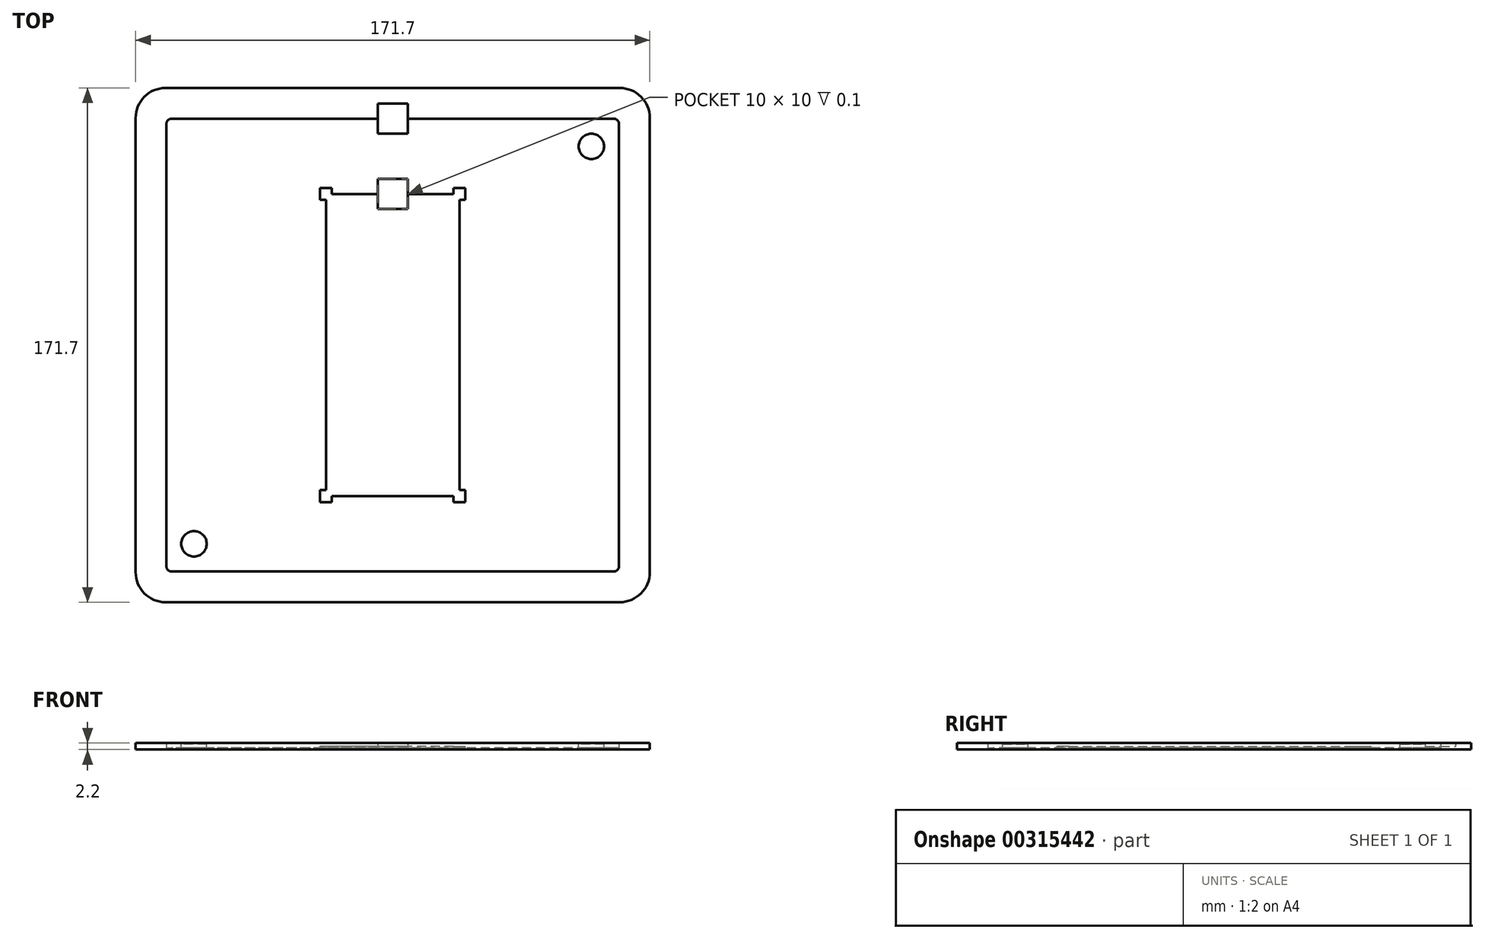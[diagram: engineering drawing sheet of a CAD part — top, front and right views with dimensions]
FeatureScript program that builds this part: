
annotation { "Feature Type Name" : "Feature", "Feature Type Description" : "" }
export const myFeature = defineFeature(function(context is Context, id is Id, definition is map)
    precondition{}
    {
        {
            var Q0;
            Q0=qCreatedBy(makeId("Top.planeOp"),FACE);
            var sketch = newSketch(context, id + "F0", { "sketchPlane" : qUnion([Q0])});
            skLineSegment(sketch, "E0.bottom", {"start": v(-75.85, 85.85) * mm, "end": v(75.85, 85.85) * mm});
            skLineSegment(sketch, "E0.top", {"start": v(-75.85, -85.85) * mm, "end": v(75.85, -85.85) * mm});
            skLineSegment(sketch, "E0.left", {"start": v(-85.85, 75.85) * mm, "end": v(-85.85, -75.85) * mm});
            skLineSegment(sketch, "E0.right", {"start": v(85.85, 75.85) * mm, "end": v(85.85, -75.85) * mm});
            skPoint(sketch, "E0.middle", {"position": v(0, 0) * mm});
            skLineSegment(sketch, "E1.bottom", {"start": v(-20.3, 50.45) * mm, "end": v(20.3, 50.45) * mm});
            skLineSegment(sketch, "E1.top", {"start": v(-20.3, -50.45) * mm, "end": v(20.3, -50.45) * mm});
            skLineSegment(sketch, "E1.left", {"start": v(-22.3, 48.45) * mm, "end": v(-22.3, -48.45) * mm});
            skLineSegment(sketch, "E1.right", {"start": v(22.3, 48.45) * mm, "end": v(22.3, -48.45) * mm});
            skPoint(sketch, "E2", {"position": v(0, 50.45) * mm});
            skPoint(sketch, "E3", {"position": v(-22.3, 0) * mm});
            skLineSegment(sketch, "E4.bottom", {"start": v(73.8, 75.6) * mm, "end": v(-73.8, 75.6) * mm});
            skLineSegment(sketch, "E4.top", {"start": v(73.8, -75.6) * mm, "end": v(-73.8, -75.6) * mm});
            skLineSegment(sketch, "E4.left", {"start": v(75.6, 73.8) * mm, "end": v(75.6, -73.8) * mm});
            skLineSegment(sketch, "E4.right", {"start": v(-75.6, 73.8) * mm, "end": v(-75.6, -73.8) * mm});
            skPoint(sketch, "E5.visualSharp", {"position": v(-85.85, 85.85) * mm});
            skArc(sketch, "E5.filletArc", {"start": v(-75.85, 85.85) * mm, "mid": v(-82.92, 82.92) * mm, "end": v(-85.85, 75.85) * mm});
            skPoint(sketch, "E6.visualSharp", {"position": v(-85.85, -85.85) * mm});
            skArc(sketch, "E6.filletArc", {"start": v(-85.85, -75.85) * mm, "mid": v(-82.92, -82.92) * mm, "end": v(-75.85, -85.85) * mm});
            skPoint(sketch, "E7.visualSharp", {"position": v(85.85, -85.85) * mm});
            skArc(sketch, "E7.filletArc", {"start": v(75.85, -85.85) * mm, "mid": v(82.92, -82.92) * mm, "end": v(85.85, -75.85) * mm});
            skPoint(sketch, "E8.visualSharp", {"position": v(85.85, 85.85) * mm});
            skArc(sketch, "E8.filletArc", {"start": v(85.85, 75.85) * mm, "mid": v(82.92, 82.92) * mm, "end": v(75.85, 85.85) * mm});
            skPoint(sketch, "E9.visualSharp", {"position": v(-75.6, 75.6) * mm});
            skArc(sketch, "E9.filletArc", {"start": v(-73.8, 75.6) * mm, "mid": v(-75.07, 75.07) * mm, "end": v(-75.6, 73.8) * mm});
            skPoint(sketch, "E10.visualSharp", {"position": v(75.6, 75.6) * mm});
            skArc(sketch, "E10.filletArc", {"start": v(75.6, 73.8) * mm, "mid": v(75.07, 75.07) * mm, "end": v(73.8, 75.6) * mm});
            skPoint(sketch, "E11.visualSharp", {"position": v(75.6, -75.6) * mm});
            skArc(sketch, "E11.filletArc", {"start": v(73.8, -75.6) * mm, "mid": v(75.07, -75.07) * mm, "end": v(75.6, -73.8) * mm});
            skPoint(sketch, "E12.visualSharp", {"position": v(-75.6, -75.6) * mm});
            skArc(sketch, "E12.filletArc", {"start": v(-75.6, -73.8) * mm, "mid": v(-75.07, -75.07) * mm, "end": v(-73.8, -75.6) * mm});
            skLineSegment(sketch, "E13.bottom", {"start": v(5, 70.6) * mm, "end": v(-5, 70.6) * mm});
            skLineSegment(sketch, "E13.top", {"start": v(5, 80.6) * mm, "end": v(-5, 80.6) * mm});
            skLineSegment(sketch, "E13.left", {"start": v(5, 70.6) * mm, "end": v(5, 80.6) * mm});
            skLineSegment(sketch, "E13.right", {"start": v(-5, 70.6) * mm, "end": v(-5, 80.6) * mm});
            skPoint(sketch, "E13.middle", {"position": v(0, 75.6) * mm});
            skLineSegment(sketch, "E14.bottom", {"start": v(-5, 55.45) * mm, "end": v(5, 55.45) * mm});
            skLineSegment(sketch, "E14.top", {"start": v(-5, 45.45) * mm, "end": v(5, 45.45) * mm});
            skLineSegment(sketch, "E14.left", {"start": v(-5, 55.45) * mm, "end": v(-5, 45.45) * mm});
            skLineSegment(sketch, "E14.right", {"start": v(5, 55.45) * mm, "end": v(5, 45.45) * mm});
            skLineSegment(sketch, "E15.bottom", {"start": v(24.3, 52.45) * mm, "end": v(20.3, 52.45) * mm});
            skLineSegment(sketch, "E15.top", {"start": v(24.3, 48.45) * mm, "end": v(22.3, 48.45) * mm});
            skLineSegment(sketch, "E15.left", {"start": v(24.3, 52.45) * mm, "end": v(24.3, 48.45) * mm});
            skLineSegment(sketch, "E15.right", {"start": v(20.3, 52.45) * mm, "end": v(20.3, 50.45) * mm});
            skPoint(sketch, "E15.middle", {"position": v(22.3, 50.45) * mm});
            skLineSegment(sketch, "E16", {"start": v(0, 50.45) * mm, "end": v(0, 38.86) * mm, "construction": true});
            skPoint(sketch, "E16.endSnap0", {"position": v(0, 45.45) * mm});
            skLineSegment(sketch, "E17", {"start": v(0, 0) * mm, "end": v(8.34, 0) * mm, "construction": true});
            skLineSegment(sketch, "E18.MirrorCS", {"start": v(-24.3, 52.45) * mm, "end": v(-24.3, 48.45) * mm});
            skLineSegment(sketch, "E19.MirrorCS", {"start": v(-24.3, 48.45) * mm, "end": v(-22.3, 48.45) * mm});
            skLineSegment(sketch, "E20.MirrorCS", {"start": v(-24.3, 52.45) * mm, "end": v(-20.3, 52.45) * mm});
            skLineSegment(sketch, "E21.MirrorCS", {"start": v(-20.3, 52.45) * mm, "end": v(-20.3, 50.45) * mm});
            skLineSegment(sketch, "E22.MirrorCS", {"start": v(24.3, -52.45) * mm, "end": v(24.3, -48.45) * mm});
            skLineSegment(sketch, "E23.MirrorCS", {"start": v(24.3, -48.45) * mm, "end": v(22.3, -48.45) * mm});
            skLineSegment(sketch, "E24.MirrorCS", {"start": v(20.3, -52.45) * mm, "end": v(20.3, -50.45) * mm});
            skLineSegment(sketch, "E25.MirrorCS", {"start": v(24.3, -52.45) * mm, "end": v(20.3, -52.45) * mm});
            skLineSegment(sketch, "E26.MirrorCS", {"start": v(-20.3, -52.45) * mm, "end": v(-20.3, -50.45) * mm});
            skLineSegment(sketch, "E27.MirrorCS", {"start": v(-24.3, -48.45) * mm, "end": v(-22.3, -48.45) * mm});
            skLineSegment(sketch, "E28.MirrorCS", {"start": v(-24.3, -52.45) * mm, "end": v(-20.3, -52.45) * mm});
            skLineSegment(sketch, "E29.MirrorCS", {"start": v(-24.3, -52.45) * mm, "end": v(-24.3, -48.45) * mm});
            skPoint(sketch, "E30.orphan", {"position": v(-22.3, 50.45) * mm});
            skPoint(sketch, "E31.orphan", {"position": v(-20.3, 48.45) * mm});
            skPoint(sketch, "E32.orphan", {"position": v(20.3, 48.45) * mm});
            skPoint(sketch, "E33.orphan", {"position": v(20.3, -48.45) * mm});
            skPoint(sketch, "E34.orphan", {"position": v(-22.3, -50.45) * mm});
            skPoint(sketch, "E35.orphan", {"position": v(-20.3, -48.45) * mm});
            skSolve(sketch);
        }
        {
            var Q0;
            Q0=makeQuery(id+"F0.imprint","IMPRINT",FACE,{"disambiguationData":[TD([[makeQuery(id+"F0.imprint","IMPRINT",EDGE,{"derivedFrom":sQuery(id+"F0.wireOp",EDGE,"E0.bottom")}),-1.0]])]});
            var Q1;
            Q1=makeQuery(id+"F0.imprint","IMPRINT",FACE,{"disambiguationData":[TD([[makeQuery(id+"F0.imprint","IMPRINT",EDGE,{"derivedFrom":sQuery(id+"F0.wireOp",EDGE,"E1.bottom")}),1.0]])]});
            var Q2;
            Q2=makeQuery(id+"F0.imprint","IMPRINT",FACE,{"disambiguationData":[TD([[makeQuery(id+"F0.imprint","IMPRINT",EDGE,{"derivedFrom":sQuery(id+"F0.wireOp",EDGE,"E1.bottom")}),-1.0]])]});
            var Q3;
            {var subQ5=sQuery(id+"F0.wireOp",EDGE,"E13.top");Q3=makeQuery(id+"F0.imprint","IMPRINT",FACE,{"disambiguationData":[TD([[makeQuery(id+"F0.imprint","IMPRINT",EDGE,{"derivedFrom":subQ5}),1.0]])]});}
            var Q4;
            {var subQ5=sQuery(id+"F0.wireOp",EDGE,"E14.bottom");Q4=makeQuery(id+"F0.imprint","IMPRINT",FACE,{"disambiguationData":[TD([[makeQuery(id+"F0.imprint","IMPRINT",EDGE,{"derivedFrom":subQ5}),-1.0]])]});}
            var Q5;
            {var subQ5=sQuery(id+"F0.wireOp",EDGE,"E13.bottom");Q5=makeQuery(id+"F0.imprint","IMPRINT",FACE,{"disambiguationData":[TD([[makeQuery(id+"F0.imprint","IMPRINT",EDGE,{"derivedFrom":subQ5}),-1.0]])]});}
            var Q6;
            {var subQ5=sQuery(id+"F0.wireOp",EDGE,"E14.top");Q6=makeQuery(id+"F0.imprint","IMPRINT",FACE,{"disambiguationData":[TD([[makeQuery(id+"F0.imprint","IMPRINT",EDGE,{"derivedFrom":subQ5}),1.0]])]});}
            extrude(context, id + "F1", {"entities" : qUnion([Q0, Q1, Q2, Q3, Q4, Q5, Q6]), "depth" : 1 * mm});
        }
        {
            var Q0;
            Q0=makeQuery(id+"F0.imprint","IMPRINT",FACE,{"disambiguationData":[TD([[makeQuery(id+"F0.imprint","IMPRINT",EDGE,{"derivedFrom":sQuery(id+"F0.wireOp",EDGE,"E0.bottom")}),-1.0]])]});
            var Q1;
            {var subQ5=sQuery(id+"F0.wireOp",EDGE,"E13.top");Q1=makeQuery(id+"F0.imprint","IMPRINT",FACE,{"disambiguationData":[TD([[makeQuery(id+"F0.imprint","IMPRINT",EDGE,{"derivedFrom":subQ5}),1.0]])]});}
            extrude(context, id + "F2", {"entities" : qUnion([Q0, Q1]), "operationType" : NewBodyOperationType.ADD, "depth" : (1 + 0.8 + 0.4) * mm});
        }
        {
            var Q0;
            Q0=makeQuery(id+"F0.imprint","IMPRINT",FACE,{"disambiguationData":[TD([[makeQuery(id+"F0.imprint","IMPRINT",EDGE,{"derivedFrom":sQuery(id+"F0.wireOp",EDGE,"E1.bottom")}),1.0]])]});
            var Q1;
            {var subQ5=sQuery(id+"F0.wireOp",EDGE,"E13.bottom");Q1=makeQuery(id+"F0.imprint","IMPRINT",FACE,{"disambiguationData":[TD([[makeQuery(id+"F0.imprint","IMPRINT",EDGE,{"derivedFrom":subQ5}),-1.0]])]});}
            var Q2;
            {var subQ5=sQuery(id+"F0.wireOp",EDGE,"E14.bottom");Q2=makeQuery(id+"F0.imprint","IMPRINT",FACE,{"disambiguationData":[TD([[makeQuery(id+"F0.imprint","IMPRINT",EDGE,{"derivedFrom":subQ5}),-1.0]])]});}
            extrude(context, id + "F3", {"entities" : qUnion([Q0, Q1, Q2]), "operationType" : NewBodyOperationType.ADD, "depth" : (1 + 0.8) * mm});
        }
        {
            var Q0;
            {var subQ5=sQuery(id+"F0.wireOp",EDGE,"E13.top");Q0=makeQuery(id+"F0.imprint","IMPRINT",FACE,{"disambiguationData":[TD([[makeQuery(id+"F0.imprint","IMPRINT",EDGE,{"derivedFrom":subQ5}),1.0]])]});}
            var Q1;
            {var subQ5=sQuery(id+"F0.wireOp",EDGE,"E13.bottom");Q1=makeQuery(id+"F0.imprint","IMPRINT",FACE,{"disambiguationData":[TD([[makeQuery(id+"F0.imprint","IMPRINT",EDGE,{"derivedFrom":subQ5}),-1.0]])]});}
            var Q2;
            Q2=makeQuery(id+"F2.opExtrude","CAP_FACE",FACE,{"disambiguationData":[OSD([sQuery(id+"F0.wireOp",EDGE,"E0.bottom"),sQuery(id+"F0.wireOp",EDGE,"E0.top"),sQuery(id+"F0.wireOp",EDGE,"E0.left"),sQuery(id+"F0.wireOp",EDGE,"E0.right"),sQuery(id+"F0.wireOp",EDGE,"E4.bottom"),sQuery(id+"F0.wireOp",EDGE,"E4.top"),sQuery(id+"F0.wireOp",EDGE,"E4.left"),sQuery(id+"F0.wireOp",EDGE,"E4.right"),sQuery(id+"F0.wireOp",EDGE,"E5.filletArc"),sQuery(id+"F0.wireOp",EDGE,"E6.filletArc"),sQuery(id+"F0.wireOp",EDGE,"E7.filletArc"),sQuery(id+"F0.wireOp",EDGE,"E8.filletArc"),sQuery(id+"F0.wireOp",EDGE,"E9.filletArc"),sQuery(id+"F0.wireOp",EDGE,"E10.filletArc"),sQuery(id+"F0.wireOp",EDGE,"E11.filletArc"),sQuery(id+"F0.wireOp",EDGE,"E12.filletArc")])],"isStart":false});
            extrude(context, id + "F4", {"entities" : qUnion([Q0, Q1]), "operationType" : NewBodyOperationType.REMOVE, "endBound" : BoundingType.UP_TO_SURFACE, "endBoundEntityFace" : qUnion([Q2]), "depth" : 25 * mm, "hasSecondDirection" : true, "secondDirectionOppositeDirection" : true, "secondDirectionDepth" : -1 * mm});
        }
        {
            var Q0;
            {var subQ5=sQuery(id+"F0.wireOp",EDGE,"E14.bottom");Q0=makeQuery(id+"F0.imprint","IMPRINT",FACE,{"disambiguationData":[TD([[makeQuery(id+"F0.imprint","IMPRINT",EDGE,{"derivedFrom":subQ5}),-1.0]])]});}
            var Q1;
            {var subQ5=sQuery(id+"F0.wireOp",EDGE,"E14.top");Q1=makeQuery(id+"F0.imprint","IMPRINT",FACE,{"disambiguationData":[TD([[makeQuery(id+"F0.imprint","IMPRINT",EDGE,{"derivedFrom":subQ5}),1.0]])]});}
            var Q2;
            Q2=makeQuery(id+"F3.opExtrude","CAP_FACE",FACE,{"disambiguationData":[OSD([sQuery(id+"F0.wireOp",EDGE,"E1.bottom"),sQuery(id+"F0.wireOp",EDGE,"E1.top"),sQuery(id+"F0.wireOp",EDGE,"E1.left"),sQuery(id+"F0.wireOp",EDGE,"E1.right"),sQuery(id+"F0.wireOp",EDGE,"E4.bottom"),sQuery(id+"F0.wireOp",EDGE,"E4.top"),sQuery(id+"F0.wireOp",EDGE,"E4.left"),sQuery(id+"F0.wireOp",EDGE,"E4.right"),sQuery(id+"F0.wireOp",EDGE,"E9.filletArc"),sQuery(id+"F0.wireOp",EDGE,"E10.filletArc"),sQuery(id+"F0.wireOp",EDGE,"E11.filletArc"),sQuery(id+"F0.wireOp",EDGE,"E12.filletArc")])],"isStart":false});
            extrude(context, id + "F5", {"entities" : qUnion([Q0, Q1]), "operationType" : NewBodyOperationType.REMOVE, "endBound" : BoundingType.UP_TO_SURFACE, "endBoundEntityFace" : qUnion([Q2]), "depth" : 25 * mm, "hasSecondDirection" : true, "secondDirectionOppositeDirection" : true, "secondDirectionDepth" : -0.5 * mm});
        }
        {
            var Q0;
            Q0=makeQuery(id+"F3.opExtrude","CAP_FACE",FACE,{"disambiguationData":[OSD([sQuery(id+"F0.wireOp",EDGE,"E1.bottom"),sQuery(id+"F0.wireOp",EDGE,"E1.top"),sQuery(id+"F0.wireOp",EDGE,"E1.left"),sQuery(id+"F0.wireOp",EDGE,"E1.right"),sQuery(id+"F0.wireOp",EDGE,"E4.bottom"),sQuery(id+"F0.wireOp",EDGE,"E4.top"),sQuery(id+"F0.wireOp",EDGE,"E4.left"),sQuery(id+"F0.wireOp",EDGE,"E4.right"),sQuery(id+"F0.wireOp",EDGE,"E9.filletArc"),sQuery(id+"F0.wireOp",EDGE,"E10.filletArc"),sQuery(id+"F0.wireOp",EDGE,"E11.filletArc"),sQuery(id+"F0.wireOp",EDGE,"E12.filletArc"),sQuery(id+"F0.wireOp",EDGE,"E15.bottom"),sQuery(id+"F0.wireOp",EDGE,"E15.top"),sQuery(id+"F0.wireOp",EDGE,"E15.left"),sQuery(id+"F0.wireOp",EDGE,"E15.right"),sQuery(id+"F0.wireOp",EDGE,"E18.MirrorCS"),sQuery(id+"F0.wireOp",EDGE,"E19.MirrorCS"),sQuery(id+"F0.wireOp",EDGE,"E20.MirrorCS"),sQuery(id+"F0.wireOp",EDGE,"E21.MirrorCS"),sQuery(id+"F0.wireOp",EDGE,"E22.MirrorCS"),sQuery(id+"F0.wireOp",EDGE,"E23.MirrorCS"),sQuery(id+"F0.wireOp",EDGE,"E24.MirrorCS"),sQuery(id+"F0.wireOp",EDGE,"E25.MirrorCS"),sQuery(id+"F0.wireOp",EDGE,"E26.MirrorCS"),sQuery(id+"F0.wireOp",EDGE,"E27.MirrorCS"),sQuery(id+"F0.wireOp",EDGE,"E28.MirrorCS"),sQuery(id+"F0.wireOp",EDGE,"E29.MirrorCS")])],"isStart":false});
            var sketch = newSketch(context, id + "F6", { "sketchPlane" : qUnion([Q0])});
            skLineSegment(sketch, "E36.0", {"start": v(-5, 75.6) * mm, "end": v(-73.8, 75.6) * mm, "construction": true});
            skLineSegment(sketch, "E36.1", {"start": v(-75.6, 73.8) * mm, "end": v(-75.6, -73.8) * mm, "construction": true});
            skCircle(sketch, "E37", {"center": v(-66.35, 66.35) * mm, "radius": 4.25 * mm});
            skLineSegment(sketch, "E38", {"start": v(0, 0) * mm, "end": v(0, 11.73) * mm, "construction": true});
            skLineSegment(sketch, "E39", {"start": v(0, 0) * mm, "end": v(17.65, 0) * mm, "construction": true});
            skCircle(sketch, "E40.MirrorC", {"center": v(66.35, 66.35) * mm, "radius": 4.25 * mm});
            skCircle(sketch, "E41.MirrorC", {"center": v(66.35, -66.35) * mm, "radius": 4.25 * mm});
            skCircle(sketch, "E42.MirrorC", {"center": v(-66.35, -66.35) * mm, "radius": 4.25 * mm});
            skSolve(sketch);
        }
        {
            var Q0;
            Q0=makeQuery(id+"F6.imprint","IMPRINT",FACE,{"disambiguationData":[TD([[makeQuery(id+"F6.imprint","IMPRINT",EDGE,{"derivedFrom":sQuery(id+"F6.wireOp",EDGE,"E37")}),1.0]])]});
            var Q1;
            Q1=makeQuery(id+"F6.imprint","IMPRINT",FACE,{"disambiguationData":[TD([[makeQuery(id+"F6.imprint","IMPRINT",EDGE,{"derivedFrom":sQuery(id+"F6.wireOp",EDGE,"E40.MirrorC")}),-1.0]])]});
            var Q2;
            Q2=makeQuery(id+"F6.imprint","IMPRINT",FACE,{"disambiguationData":[TD([[makeQuery(id+"F6.imprint","IMPRINT",EDGE,{"derivedFrom":sQuery(id+"F6.wireOp",EDGE,"E41.MirrorC")}),1.0]])]});
            var Q3;
            Q3=makeQuery(id+"F6.imprint","IMPRINT",FACE,{"disambiguationData":[TD([[makeQuery(id+"F6.imprint","IMPRINT",EDGE,{"derivedFrom":sQuery(id+"F6.wireOp",EDGE,"E42.MirrorC")}),-1.0]])]});
            extrude(context, id + "F7", {"entities" : qUnion([Q0, Q1, Q2, Q3]), "operationType" : NewBodyOperationType.REMOVE, "oppositeDirection" : true, "depth" : 1.2 * mm});
        }
    });
